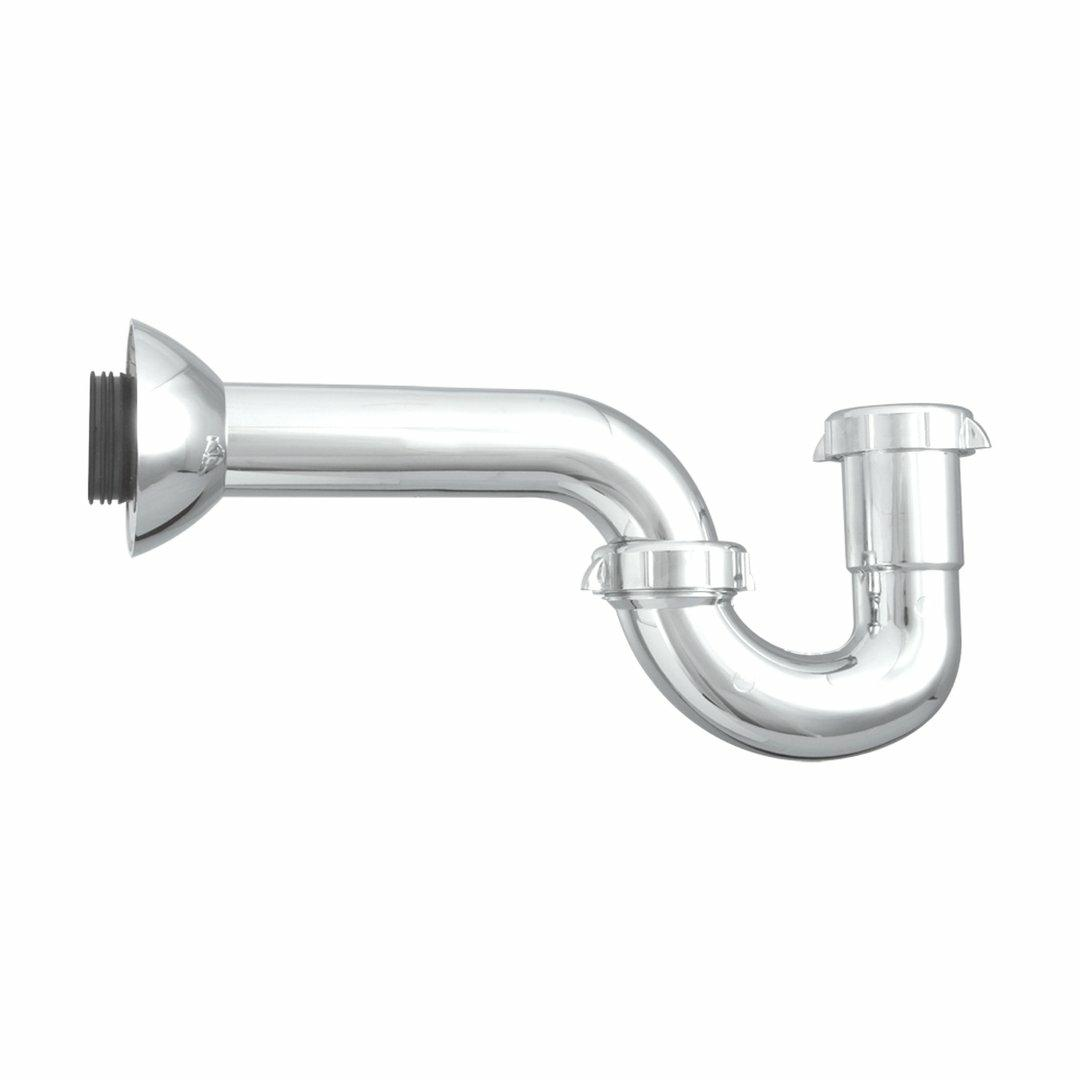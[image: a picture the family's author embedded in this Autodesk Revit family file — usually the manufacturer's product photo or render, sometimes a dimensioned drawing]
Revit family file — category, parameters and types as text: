
# Revit family: BIM_L1-3080-11
name_source: partatom
category: Aparatos sanitarios
units: mm (PartAtom-declared; Revit-internal decimal feet)

## family parameters
Activar corte en vistas = No
Anfitrión = Cara
Compartido = No
Corte con vacíos al cargar = No
Cota de conector redondo = Usar diámetro
Mantener orientación de anotación = No
Número OmniClass = 23.31.11.00
Punto de cálculo de habitación = No
Tipo de pieza = Normal

## types (1)
- L1-3080-11
    Acabado = Cepillado, Brillante
    Alto = 190 mm
    Ancho = 1200 mm  [stored 3.93701 ft]
    Conexión AC = Sí
    Conexión AF = Sí
    Conexión de residuos = No
    Conexión de ventilación = No
    Date Modified = 08-08-2025
    Descripción = Lavaplatos en acero
    Elevación por defecto = 0 mm  [stored 0 ft]
    Fabricante = Gricol
    Garantia Especifica = 5 años
    Imagen de tipo = FOTO-KIT LAVAPLATOS EN ACERO POCETA IZQUIERDA 120 x 50 cm.jpg
    Largo = 510 mm
    Link Ficha Tecnica = https://infotecnica.gricol.com
    Material = Acero inoxidable
    Modelo = L1-3080-11
    Nota clave = Lavaplatos para instalacion de griferia con unica perforacion
    Peso = 4.00 kg
    Product Name = Lavaplatos De Sobreponer Poceta Izquierda 120 X 50 Cm Con Complementos
    Resistencia a Corrosión = Si
    Sitio web = https://www.gricol.com
    Tipo de Uso = Residencial
    URL = https://www.gricol.com

note: [stored X ft] marks values corroborated as IEEE doubles in the binary element streams (Revit-internal decimal feet)

## geometry (parser evidence)
native form markers: Blend x2, Sweep x14
no freeform markers — native parametric forms only
